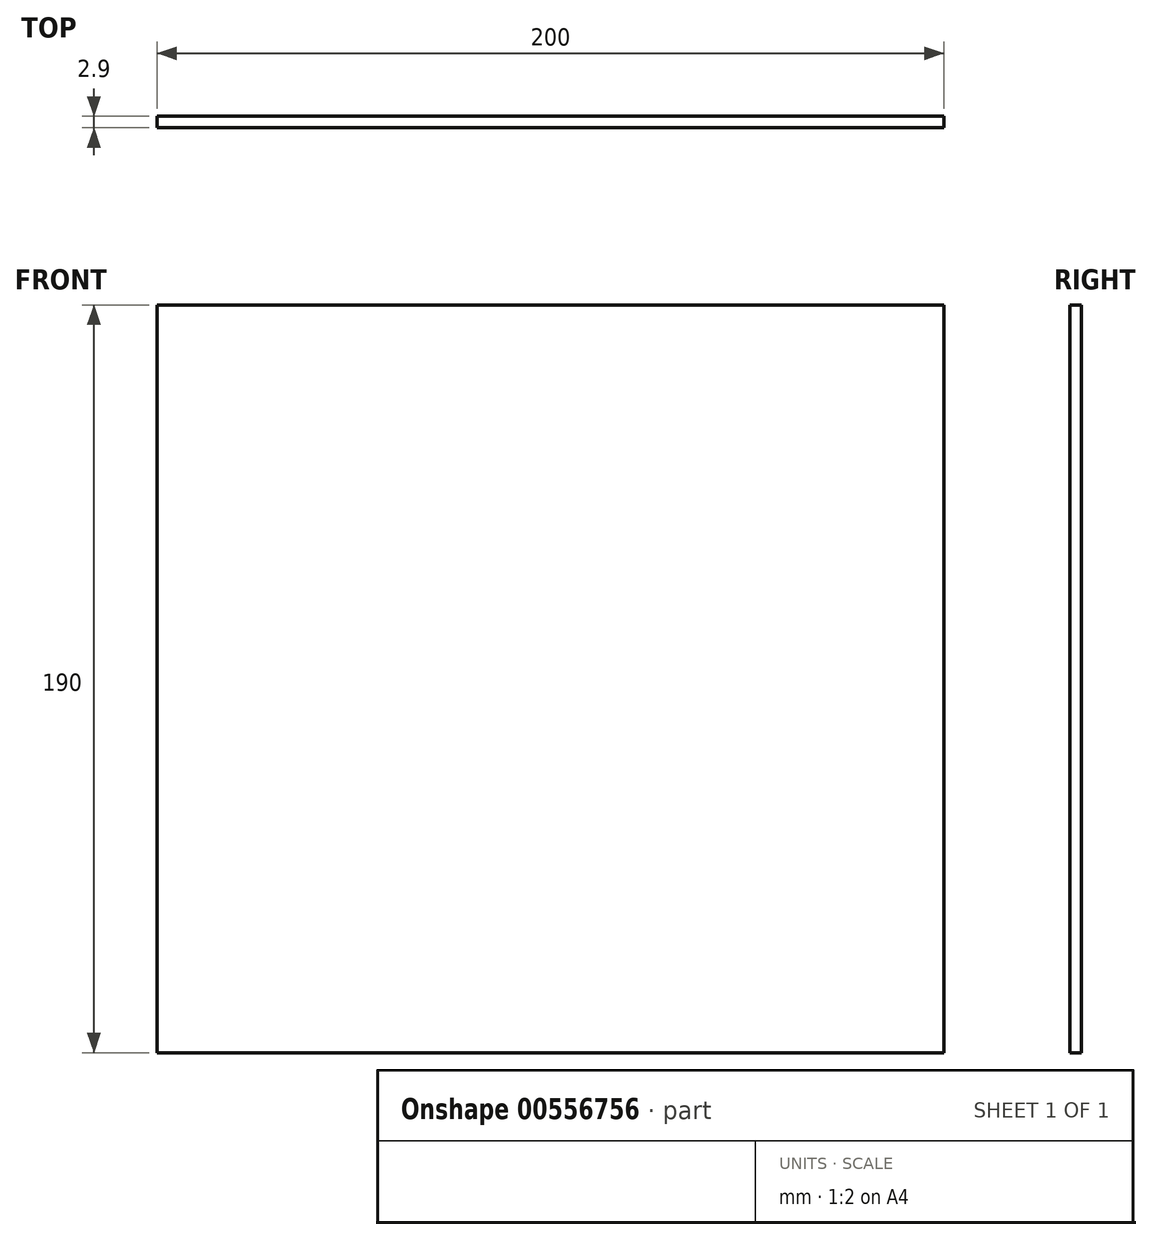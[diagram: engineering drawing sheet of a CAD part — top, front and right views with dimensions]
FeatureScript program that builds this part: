
annotation { "Feature Type Name" : "Feature", "Feature Type Description" : "" }
export const myFeature = defineFeature(function(context is Context, id is Id, definition is map)
    precondition{}
    {
        {
            var Q0;
            Q0=qCreatedBy(makeId("Front.planeOp"),FACE);
            var sketch = newSketch(context, id + "F0", { "sketchPlane" : qUnion([Q0])});
            skLineSegment(sketch, "E0", {"start": v(0, 0) * mm, "end": v(0, -190) * mm});
            skLineSegment(sketch, "E1", {"start": v(0, -190) * mm, "end": v(200, -190) * mm});
            skLineSegment(sketch, "E2", {"start": v(200, -190) * mm, "end": v(200, 0) * mm});
            skLineSegment(sketch, "E3", {"start": v(200, 0) * mm, "end": v(0, 0) * mm});
            skSolve(sketch);
        }
        {
            var Q0;
            Q0=makeQuery(id+"F0.imprint","IMPRINT",FACE,{"disambiguationData":[TD([[makeQuery(id+"F0.imprint","IMPRINT",EDGE,{"derivedFrom":sQuery(id+"F0.wireOp",EDGE,"E0")}),1.0]])]});
            extrude(context, id + "F1", {"entities" : qUnion([Q0]), "depth" : 2.9 * mm, "offsetDistance" : 25 * mm});
        }
    });
